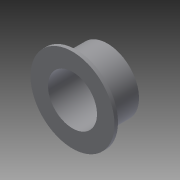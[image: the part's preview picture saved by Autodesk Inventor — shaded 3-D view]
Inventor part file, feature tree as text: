
AUTODESK INVENTOR PART (.ipt)
format: ipt  version: 2014 (Build 180170000, 170)  size: 90,112 bytes
history: native  units: mm
features: extrude x2, sketch x2
ambient origin geometry x8: Origin, YZ Plane, XZ Plane, XY Plane, X Axis, Y Axis, Z Axis, Center Point
bodies: Solid1 (feature_tree)
feature tree (4):
  extrude  "Extrusion1"  Depth=9.0mm
  extrude  "Extrusion2"  Depth=0.5mm
  sketch  "Sketch1"  dims[d0=7.0mm d1=9.0mm]
  sketch  "Sketch2"  dims[d2=5.0mm d3=0.0mm d4=12.0mm d5=0.5mm d6=0.0mm]
